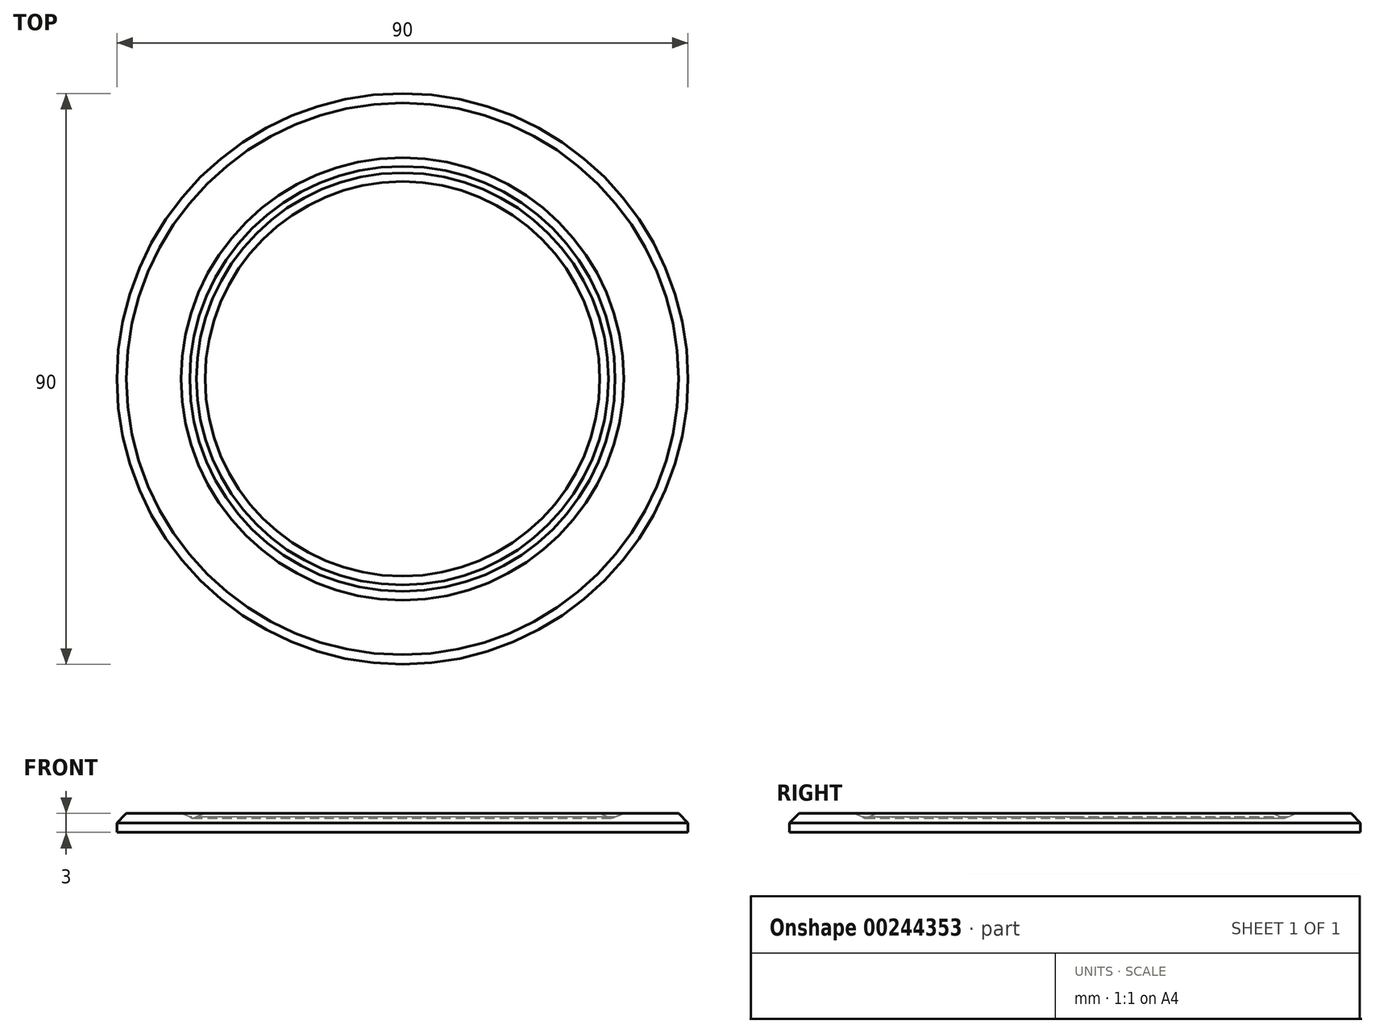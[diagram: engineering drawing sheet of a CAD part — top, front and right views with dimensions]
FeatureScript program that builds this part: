
annotation { "Feature Type Name" : "Feature", "Feature Type Description" : "" }
export const myFeature = defineFeature(function(context is Context, id is Id, definition is map)
    precondition{}
    {
        {
            var Q0;
            Q0=qCreatedBy(makeId("Front.planeOp"),FACE);
            var sketch = newSketch(context, id + "F0", { "sketchPlane" : qUnion([Q0])});
            skLineSegment(sketch, "E0", {"start": v(0, 0) * mm, "end": v(0, 40) * mm, "construction": true});
            skLineSegment(sketch, "E1.bottom", {"start": v(0, 0) * mm, "end": v(45, 0) * mm});
            skLineSegment(sketch, "E1.top", {"start": v(0, 3) * mm, "end": v(45, 3) * mm});
            skLineSegment(sketch, "E1.left", {"start": v(0, 0) * mm, "end": v(0, 3) * mm});
            skLineSegment(sketch, "E1.right", {"start": v(45, 0) * mm, "end": v(45, 3) * mm});
            skPoint(sketch, "E2", {"position": v(39, 3) * mm});
            skPoint(sketch, "E3", {"position": v(33, 3) * mm});
            skPoint(sketch, "E4", {"position": v(27, 3) * mm});
            skPoint(sketch, "E5", {"position": v(21, 3) * mm});
            skPoint(sketch, "E6", {"position": v(15, 3) * mm});
            skPoint(sketch, "E7", {"position": v(9, 3) * mm});
            skPoint(sketch, "E8", {"position": v(3, 3) * mm});
            skLineSegment(sketch, "E9.bottom", {"start": v(0, 3) * mm, "end": v(3, 3) * mm});
            skLineSegment(sketch, "E9.top", {"start": v(0, 3) * mm, "end": v(3, 3) * mm, "construction": true});
            skLineSegment(sketch, "E9.left", {"start": v(0, 3) * mm, "end": v(0, 3) * mm});
            skLineSegment(sketch, "E9.right", {"start": v(3, 3) * mm, "end": v(3, 3) * mm});
            skLineSegment(sketch, "E10.bottom", {"start": v(3, 3) * mm, "end": v(0, 3) * mm, "construction": true});
            skLineSegment(sketch, "E10.top", {"start": v(3, 34) * mm, "end": v(0, 34) * mm, "construction": true});
            skLineSegment(sketch, "E10.left", {"start": v(3, 3) * mm, "end": v(3, 34) * mm});
            skLineSegment(sketch, "E10.right", {"start": v(0, 3) * mm, "end": v(0, 34) * mm});
            skLineSegment(sketch, "E11", {"start": v(33, 3) * mm, "end": v(-7.8, 30.52) * mm, "construction": true});
            skLineSegment(sketch, "E12", {"start": v(33, 3) * mm, "end": v(33, 35.23) * mm});
            skLineSegment(sketch, "E13", {"start": v(3, 23.24) * mm, "end": v(0, 23.24) * mm});
            skCircle(sketch, "E14", {"center": v(33, 3) * mm, "radius": 0.75 * mm});
            skSolve(sketch);
        }
        {
            var Q0;
            Q0=makeQuery(id+"F0.imprint","IMPRINT",FACE,{"disambiguationData":[TD([[makeQuery(id+"F0.imprint","IMPRINT",EDGE,{"derivedFrom":sQuery(id+"F0.wireOp",EDGE,"E1.bottom")}),1.0]])]});
            var Q1;
            {var subQ0=sQuery(id+"F0.wireOp",EDGE,"E9.bottom");Q1=makeQuery(id+"F0.imprint","IMPRINT",FACE,{"disambiguationData":[TD([[makeQuery(id+"F0.imprint","IMPRINT",EDGE,{"derivedFrom":subQ0}),1.0]])]});}
            var Q2;
            Q2=sQuery(id+"F0.wireOp",EDGE,"E9.top");
            var Q3;
            Q3=sQuery(id+"F0.wireOp",EDGE,"E1.bottom");
            var Q4;
            Q4=sQuery(id+"F0.wireOp",EDGE,"E1.right");
            var Q5;
            Q5=sQuery(id+"F0.wireOp",EDGE,"E1.top");
            var Q6;
            Q6=sQuery(id+"F0.wireOp",EDGE,"E10.left");
            var Q7;
            Q7=sQuery(id+"F0.wireOp",EDGE,"E13");
            var Q8;
            Q8=sQuery(id+"F0.wireOp",EDGE,"E10.right");
            revolve(context, id + "F1", {"entities" : qUnion([Q0, Q1]), "surfaceEntities" : qUnion([Q2, Q3, Q4, Q5, Q6, Q7]), "axis" : qUnion([Q8]), "revolveType" : RevolveType.FULL});
        }
        {
            var Q0;
            Q0=makeQuery(id+"F1.opRevolve","SWEPT_EDGE",EDGE,{"disambiguationData":[OSD([sQuery(id+"F0.wireOp",EDGE,"E1.top"),sQuery(id+"F0.wireOp",EDGE,"E1.right")])]});
            chamfer(context, id + "F2", {"entities" : qUnion([Q0]), "width" : 1.5 * mm, "tangentPropagation" : true});
        }
        {
            var Q0;
            Q0=makeQuery(id+"F1.opRevolve","SWEPT_EDGE",EDGE,{"disambiguationData":[OSD([sQuery(id+"F0.wireOp",EDGE,"E1.top"),sQuery(id+"F0.wireOp",EDGE,"E9.bottom"),sQuery(id+"F0.wireOp",EDGE,"E10.left")])]});
            chamfer(context, id + "F3", {"entities" : qUnion([Q0]), "width" : 2 * mm, "tangentPropagation" : true});
        }
    });
